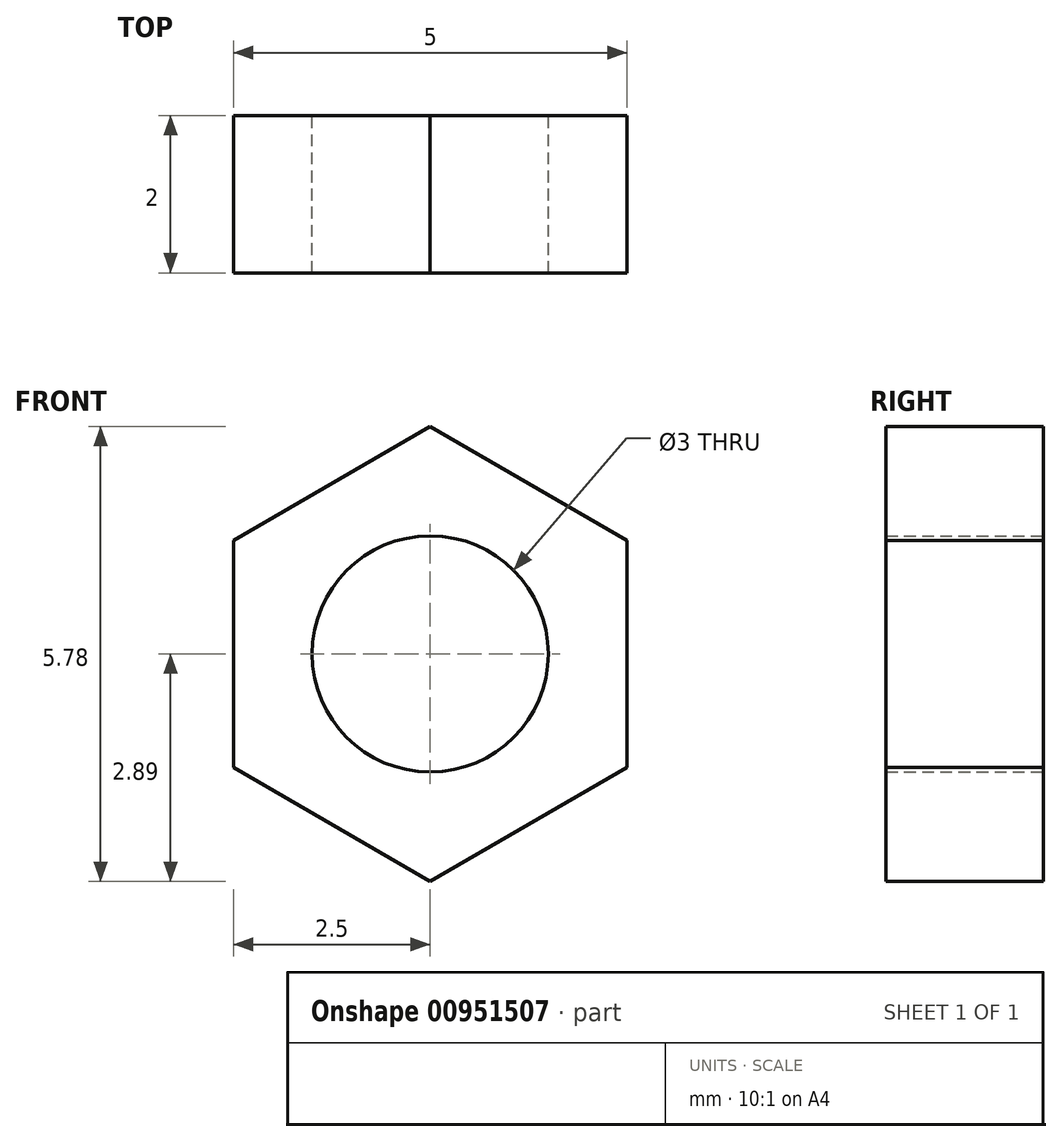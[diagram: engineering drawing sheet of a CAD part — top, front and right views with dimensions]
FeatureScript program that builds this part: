
annotation { "Feature Type Name" : "Feature", "Feature Type Description" : "" }
export const myFeature = defineFeature(function(context is Context, id is Id, definition is map)
    precondition{}
    {
        {
            var Q0;
            Q0=qCreatedBy(makeId("Front.planeOp"),FACE);
            var sketch = newSketch(context, id + "F0", { "sketchPlane" : qUnion([Q0])});
            skCircle(sketch, "E0", {"center": v(0, 0) * mm, "radius": 1.5 * mm});
            skCircle(sketch, "E1.cCircle", {"center": v(0, 0) * mm, "radius": 2.5 * mm, "construction": true});
            skLineSegment(sketch, "E1.0", {"start": v(-2.5, -1.44) * mm, "end": v(-2.5, 1.44) * mm});
            skLineSegment(sketch, "E1.1", {"start": v(-2.5, 1.44) * mm, "end": v(0, 2.89) * mm});
            skLineSegment(sketch, "E1.2", {"start": v(0, 2.89) * mm, "end": v(2.5, 1.44) * mm});
            skLineSegment(sketch, "E1.3", {"start": v(2.5, 1.44) * mm, "end": v(2.5, -1.44) * mm});
            skLineSegment(sketch, "E1.4", {"start": v(2.5, -1.44) * mm, "end": v(0, -2.89) * mm});
            skLineSegment(sketch, "E1.5", {"start": v(0, -2.89) * mm, "end": v(-2.5, -1.44) * mm});
            skPoint(sketch, "E1.0.midPoint", {"position": v(-2.5, 0) * mm});
            skSolve(sketch);
        }
        {
            var Q0;
            Q0=qSketchRegion(id+"F0",true);
            extrude(context, id + "F1", {"entities" : qUnion([Q0]), "depth" : 2 * mm, "offsetDistance" : 25 * mm});
        }
    });
